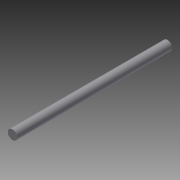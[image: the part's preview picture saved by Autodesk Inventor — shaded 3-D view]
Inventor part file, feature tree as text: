
AUTODESK INVENTOR PART (.ipt)
format: ipt  version: 2014 (Build 180170000, 170)  size: 66,048 bytes
history: native  units: in
note: dims shown in document units (in); Inventor stores cm internally (conversion verified against a paired STEP export)
features: extrude x1, sketch x1
ambient origin geometry x8: Origin, YZ Plane, XZ Plane, XY Plane, X Axis, Y Axis, Z Axis, Center Point
bodies: Solid1 (feature_tree)
feature tree (2):
  extrude  "Extrusion1"  Depth=8.25in TaperAngle=0.0deg
  sketch  "Sketch1"  dims[d0=0.5in d1=8.25in d2=0.0in]
